# Revit family: Projection_Screen-Draper_Inc.-Targa
name_source: partatom
category: Specialty Equipment
units: mm (PartAtom-declared; Revit-internal decimal feet)

## family parameters
Always vertical = Yes
Classification Number = 23.85.10.14.31
Cut with Voids When Loaded = No
Enable Cutting in Views = No
Maintain Annotation Orientation = No
Part Type = Normal
Room Calculation Point = No
Round Connector Dimension = Use Diameter
Shared = No
Work Plane-Based = No

## types (80) — shared parameters
Apparent Load = 132 VA
Case Material = Paint - Draper - White
Default Elevation = 0"
Depth = 5 1/4"
Description = Projection Screen
Frequency = 60 Hz
Manufacturer = Draper Inc.
Model = Targa
Number of Poles = 1
Product Documentation Link = http://www.draperinc.com
Product Name = Targa  Electric Projection Screen
Product Page URL = http://www.draperinc.com
Projection Screen Material = Fabric - Draper - CH1900E - Pearl White
URL = http://www.DraperInc.com
Width = 4 3/4"

## per-type parameters (varying)
| type | Border | Image Area | Image Height | Image Height Constraint | Image Length | Image Length Constraint | Length | Overall Size | Screen | Screen Drop | Voltage |
| AV Format - 12’  x 12’  - 220 V | No | 144" x 144" | 12' - 0" | 11' - 11 3/4" | 12' - 0" | 11' - 11 3/4" | 12' - 7" | 144" x 144" | 12' - 0" | 12' - 0" | 220 V |
| AV Format - 9’  x 12’  - 220 V | No | 108" x 144" | 9' - 0" | 8' - 11 3/4" | 12' - 0" | 11' - 11 3/4" | 12' - 7" | 108" x 144" | 12' - 0" | 9' - 0" | 220 V |
| AV Format - 10’  x 10’  - 220 V | No | 120" x 120" | 10' - 0" | 9' - 11 3/4" | 10' - 0" | 9' - 11 3/4" | 10' - 7" | 120" x 120" | 10' - 0" | 10' - 0" | 220 V |
| AV Format - 8’  x 10’  - 220 V | No | 96" x 120" | 8' - 0" | 7' - 11 3/4" | 10' - 0" | 9' - 11 3/4" | 10' - 7" | 96" x 120" | 10' - 0" | 8' - 0" | 220 V |
| AV Format - 9’  x 9’  - 220 V | No | 108" x 108" | 9' - 0" | 8' - 11 3/4" | 9' - 0" | 8' - 11 3/4" | 9' - 7" | 108" x 108" | 9' - 0" | 9' - 0" | 220 V |
| AV Format - 7’  x 9’  - 220 V | No | 84" x 108" | 7' - 0" | 6' - 11 3/4" | 9' - 0" | 8' - 11 3/4" | 9' - 7" | 84" x 108" | 9' - 0" | 7' - 0" | 220 V |
| AV Format - 96" x 96" - 220 V | No | 96" x 96" | 8' - 0" | 7' - 11 3/4" | 8' - 0" | 7' - 11 3/4" | 8' - 7" | 96" x 96" | 8' - 0" | 8' - 0" | 220 V |
| AV Format - 72" x 96" - 220 V | No | 72" x 96" | 6' - 0" | 5' - 11 3/4" | 8' - 0" | 7' - 11 3/4" | 8' - 7" | 72" x 96" | 8' - 0" | 6' - 0" | 220 V |
| AV Format - 84" x 84" - 220 V | No | 84" x 84" | 7' - 0" | 6' - 11 3/4" | 7' - 0" | 6' - 11 3/4" | 7' - 6 1/2" | 84" x 84" | 7' - 0" | 7' - 0" | 220 V |
| AV Format - 70" x 70" - 220 V | No | 70" x 70" | 5' - 10" | 5' - 9 3/4" | 5' - 10" | 5' - 9 3/4" | 6' - 4 1/2" | 70" x 70" | 5' - 10" | 5' - 10" | 220 V |
| AV Format - 60" x 60" - 220 V | No | 60" x 60" | 5' - 0" | 4' - 11 3/4" | 5' - 0" | 4' - 11 3/4" | 5' - 6 1/2" | 60" x 60" | 5' - 0" | 5' - 0" | 220 V |
| AV Format - 50" x 50" - 220 V | No | 50" x 50" | 4' - 2" | 4' - 1 3/4" | 4' - 2" | 4' - 1 3/4" | 4' - 8 1/2" | 50" x 50" | 4' - 2" | 4' - 2" | 220 V |
| 16:10 Format - 189" - 220 V | Yes | 100" x 160" | 8' - 4" | 8' - 4" | 13' - 4" | 13' - 4" | 14' - 3" | 105" x 164" | 13' - 8" | 8' - 9" | 220 V |
| 16:10 Format - 165" - 220 V | Yes | 87 1/2" x 140" | 7' - 3 1/2" | 7' - 3 1/2" | 11' - 8" | 11' - 8" | 12' - 7" | 92 1/2" x 144" | 12' - 0" | 7' - 8 1/2" | 220 V |
| 16:10 Format - 137" - 220 V | Yes | 72 1/2" x 116" | 6' - 0 1/2" | 6' - 0 1/2" | 9' - 8" | 9' - 8" | 10' - 7" | 76 1/2" x 120" | 10' - 0" | 6' - 4 1/2" | 220 V |
| 16:10 Format - 123" - 220 V | Yes | 65" x 104" | 5' - 5" | 5' - 5" | 8' - 8" | 8' - 8" | 9' - 7" | 69" x 108" | 9' - 0" | 5' - 9" | 220 V |
| 16:10 Format - 109" - 220 V | Yes | 57 1/2" x 92" | 4' - 9 1/2" | 4' - 9 1/2" | 7' - 8" | 7' - 8" | 8' - 7" | 69 1/2" x 96" | 8' - 0" | 5' - 9 1/2" | 220 V |
| 16:10 Format - 94" - 220 V | Yes | 50" x 80" | 4' - 2" | 4' - 2" | 6' - 8" | 6' - 8" | 7' - 6 1/2" | 62" x 83 1/2" | 6' - 11 1/2" | 5' - 2" | 220 V |
| 16:10 Format - 85" - 220 V | Yes | 45" x 72" | 3' - 9" | 3' - 9" | 6' - 0" | 6' - 0" | 6' - 9" | 57" x 74" | 6' - 2" | 4' - 9" | 220 V |
| 16:10 Format - 76" - 220 V | Yes | 40" x 64" | 3' - 4" | 3' - 4" | 5' - 4" | 5' - 4" | 6' - 4 1/2" | 52" x 69 1/2" | 5' - 9 1/2" | 4' - 4" | 220 V |
| 16:10 Format - 67" - 220 V | Yes | 35 ¬" x 56 1/2" | 2' - 11 1/4" | 2' - 11 1/4" | 4' - 8 1/2" | 4' - 8 1/2" | 5' - 6 1/2" | 47 ¬" x 59 1/2" | 4' - 11 1/2" | 3' - 11 1/4" | 220 V |
| 16:9 HDTV Format - 184" - 220 V | Yes | 90" x 160" | 7' - 6" | 7' - 6" | 13' - 4" | 13' - 4" | 14' - 3" | 95" x 164" | 13' - 8" | 7' - 11" | 220 V |
| 16:9 HDTV Format - 161" - 220 V | Yes | 79" x 140" | 6' - 7" | 6' - 7" | 11' - 8" | 11' - 8" | 12' - 7" | 84" x 144" | 12' - 0" | 7' - 0" | 220 V |
| 16:9 HDTV Format - 133" - 220 V | Yes | 65" x 116" | 5' - 5" | 5' - 5" | 9' - 8" | 9' - 8" | 10' - 7" | 69" x 120" | 10' - 0" | 5' - 9" | 220 V |
| 16:9 HDTV Format - 119" - 220 V | Yes | 58" x 104" | 4' - 10" | 4' - 10" | 8' - 8" | 8' - 8" | 9' - 7" | 62" x 108" | 9' - 0" | 5' - 2" | 220 V |
| 16:9 HDTV Format - 110" - 220 V | Yes | 54" x 96" | 4' - 6" | 4' - 6" | 8' - 0" | 8' - 0" | 8' - 11" | 66" x 100" | 8' - 4" | 5' - 6" | 220 V |
| 16:9 HDTV Format - 106" - 220 V | Yes | 52" x 92" | 4' - 4" | 4' - 4" | 7' - 8" | 7' - 8" | 8' - 7" | 64" x 96" | 8' - 0" | 5' - 4" | 220 V |
| 16:9 HDTV Format - 100" - 220 V | Yes | 49" x 87" | 4' - 1" | 4' - 1" | 7' - 3" | 7' - 3" | 8' - 2" | 61" x 91" | 7' - 7" | 5' - 1" | 220 V |
| 16:9 HDTV Format - 92" - 220 V | Yes | 45" x 80" | 3' - 9" | 3' - 9" | 6' - 8" | 6' - 8" | 7' - 6 1/2" | 57" x 83 1/2" | 6' - 11 1/2" | 4' - 9" | 220 V |
| 16:9 HDTV Format - 82" - 220 V | Yes | 40 1/2" x 72" | 3' - 4 1/2" | 3' - 4 1/2" | 6' - 0" | 6' - 0" | 6' - 9" | 52 1/2" x 74" | 6' - 2" | 4' - 4 1/2" | 220 V |
| 16:9 HDTV Format - 73" - 220 V | Yes | 36" x 64" | 3' - 0" | 3' - 0" | 5' - 4" | 5' - 4" | 6' - 4 1/2" | 48" x 69 1/2" | 5' - 9 1/2" | 4' - 0" | 220 V |
| 16:9 HDTV Format - 65" - 220 V | Yes | 31 ‘ " x 56 1/2" | 2' - 6 3/4" | 2' - 6 3/4" | 4' - 8 1/2" | 4' - 8 1/2" | 5' - 6 1/2" | 43 ‘ " x 59 1/2" | 4' - 11 1/2" | 3' - 7 3/4" | 220 V |
| 4:3 NTSC/PAL Video Format - 200" - 220 V | Yes | 118" x 158" | 9' - 10" | 9' - 10" | 13' - 2" | 13' - 2" | 14' - 1" | 123" x 162" | 13' - 6" | 10' - 3" | 220 V |
| 4:3 NTSC/PAL Video Format - 15’  - 220 V | Yes | 105" x 140" | 8' - 9" | 8' - 9" | 11' - 8" | 11' - 8" | 12' - 7" | 109" x 144" | 12' - 0" | 9' - 1" | 220 V |
| 4:3 NTSC/PAL Video Format - 150" - 220 V | Yes | 87" x 116" | 7' - 3" | 7' - 3" | 9' - 8" | 9' - 8" | 10' - 7" | 92" x 120" | 10' - 0" | 7' - 8" | 220 V |
| 4:3 NTSC/PAL Video Format - 11’  - 220 V | Yes | 78" x 104" | 6' - 6" | 6' - 6" | 8' - 8" | 8' - 8" | 9' - 7" | 83" x 108" | 9' - 0" | 6' - 11" | 220 V |
| 4:3 NTSC/PAL Video Format - 10’  - 220 V | Yes | 69" x 92" | 5' - 9" | 5' - 9" | 7' - 8" | 7' - 8" | 8' - 7" | 73" x 96" | 8' - 0" | 6' - 1" | 220 V |
| 4:3 NTSC/PAL Video Format - 100" - 220 V | Yes | 60" x 80" | 5' - 0" | 5' - 0" | 6' - 8" | 6' - 8" | 7' - 6 1/2" | 64" x 83 1/2" | 6' - 11 1/2" | 5' - 4" | 220 V |
| 4:3 NTSC/PAL Video Format - 7’  - 220 V | Yes | 50" x 66 1/2" | 4' - 2" | 4' - 2" | 5' - 6 1/2" | 5' - 6 1/2" | 6' - 4 1/2" | 53 1/2" x 69 1/2" | 5' - 9 1/2" | 4' - 5 1/2" | 220 V |
| 4:3 NTSC/PAL Video Format - 6’  - 220 V | Yes | 42 1/2" x 56 1/2" | 3' - 6 1/2" | 3' - 6 1/2" | 4' - 8 1/2" | 4' - 8 1/2" | 5' - 6 1/2" | 46 1/2" x 59 1/2" | 4' - 11 1/2" | 3' - 10 1/2" | 110 V |
| AV Format - 12’  x 12’  - 110 V | No | 144" x 144" | 12' - 0" | 11' - 11 3/4" | 12' - 0" | 11' - 11 3/4" | 12' - 7" | 144" x 144" | 12' - 0" | 12' - 0" | 110 V |
| AV Format - 9’  x 12’  - 110 V | No | 108" x 144" | 9' - 0" | 8' - 11 3/4" | 12' - 0" | 11' - 11 3/4" | 12' - 7" | 108" x 144" | 12' - 0" | 9' - 0" | 110 V |
| AV Format - 10’  x 10’  - 110 V | No | 120" x 120" | 10' - 0" | 9' - 11 3/4" | 10' - 0" | 9' - 11 3/4" | 10' - 7" | 120" x 120" | 10' - 0" | 10' - 0" | 110 V |
| AV Format - 8’  x 10’  - 110 V | No | 96" x 120" | 8' - 0" | 7' - 11 3/4" | 10' - 0" | 9' - 11 3/4" | 10' - 7" | 96" x 120" | 10' - 0" | 8' - 0" | 110 V |
| AV Format - 9’  x 9’  - 110 V | No | 108" x 108" | 9' - 0" | 8' - 11 3/4" | 9' - 0" | 8' - 11 3/4" | 9' - 7" | 108" x 108" | 9' - 0" | 9' - 0" | 110 V |
| AV Format - 7’  x 9’  - 110 V | No | 84" x 108" | 7' - 0" | 6' - 11 3/4" | 9' - 0" | 8' - 11 3/4" | 9' - 7" | 84" x 108" | 9' - 0" | 7' - 0" | 110 V |
| AV Format - 96" x 96" - 110 V | No | 96" x 96" | 8' - 0" | 7' - 11 3/4" | 8' - 0" | 7' - 11 3/4" | 8' - 7" | 96" x 96" | 8' - 0" | 8' - 0" | 110 V |
| AV Format - 72" x 96" - 110 V | No | 72" x 96" | 6' - 0" | 5' - 11 3/4" | 8' - 0" | 7' - 11 3/4" | 8' - 7" | 72" x 96" | 8' - 0" | 6' - 0" | 110 V |
| AV Format - 84" x 84" - 110 V | No | 84" x 84" | 7' - 0" | 6' - 11 3/4" | 7' - 0" | 6' - 11 3/4" | 7' - 6 1/2" | 84" x 84" | 7' - 0" | 7' - 0" | 110 V |
| AV Format - 70" x 70" - 110 V | No | 70" x 70" | 5' - 10" | 5' - 9 3/4" | 5' - 10" | 5' - 9 3/4" | 6' - 4 1/2" | 70" x 70" | 5' - 10" | 5' - 10" | 110 V |
| AV Format - 60" x 60" - 110 V | No | 60" x 60" | 5' - 0" | 4' - 11 3/4" | 5' - 0" | 4' - 11 3/4" | 5' - 6 1/2" | 60" x 60" | 5' - 0" | 5' - 0" | 110 V |
| AV Format - 50" x 50" - 110 V | No | 50" x 50" | 4' - 2" | 4' - 1 3/4" | 4' - 2" | 4' - 1 3/4" | 4' - 8 1/2" | 50" x 50" | 4' - 2" | 4' - 2" | 110 V |
| 16:10 Format - 189" - 110 V | Yes | 100" x 160" | 8' - 4" | 8' - 4" | 13' - 4" | 13' - 4" | 14' - 3" | 105" x 164" | 13' - 8" | 8' - 9" | 110 V |
| 16:10 Format - 165" - 110 V | Yes | 87 1/2" x 140" | 7' - 3 1/2" | 7' - 3 1/2" | 11' - 8" | 11' - 8" | 12' - 7" | 92 1/2" x 144" | 12' - 0" | 7' - 8 1/2" | 110 V |
| 16:10 Format - 137" - 110 V | Yes | 72 1/2" x 116" | 6' - 0 1/2" | 6' - 0 1/2" | 9' - 8" | 9' - 8" | 10' - 7" | 76 1/2" x 120" | 10' - 0" | 6' - 4 1/2" | 110 V |
| 16:10 Format - 123" - 110 V | Yes | 65" x 104" | 5' - 5" | 5' - 5" | 8' - 8" | 8' - 8" | 9' - 7" | 69" x 108" | 9' - 0" | 5' - 9" | 110 V |
| 16:10 Format - 109" - 110 V | Yes | 57 1/2" x 92" | 4' - 9 1/2" | 4' - 9 1/2" | 7' - 8" | 7' - 8" | 8' - 7" | 69 1/2" x 96" | 8' - 0" | 5' - 9 1/2" | 110 V |
| 16:10 Format - 94" - 110 V | Yes | 50" x 80" | 4' - 2" | 4' - 2" | 6' - 8" | 6' - 8" | 7' - 6 1/2" | 62" x 83 1/2" | 6' - 11 1/2" | 5' - 2" | 110 V |
| 16:10 Format - 85" - 110 V | Yes | 45" x 72" | 3' - 9" | 3' - 9" | 6' - 0" | 6' - 0" | 6' - 9" | 57" x 74" | 6' - 2" | 4' - 9" | 110 V |
| 16:10 Format - 76" - 110 V | Yes | 40" x 64" | 3' - 4" | 3' - 4" | 5' - 4" | 5' - 4" | 6' - 4 1/2" | 52" x 69 1/2" | 5' - 9 1/2" | 4' - 4" | 110 V |
| 16:10 Format - 67" - 110 V | Yes | 35 ¬" x 56 1/2" | 2' - 11 1/4" | 2' - 11 1/4" | 4' - 8 1/2" | 4' - 8 1/2" | 5' - 6 1/2" | 47 ¬" x 59 1/2" | 4' - 11 1/2" | 3' - 11 1/4" | 110 V |
| 16:9 HDTV Format - 184" - 110 V | Yes | 90" x 160" | 7' - 6" | 7' - 6" | 13' - 4" | 13' - 4" | 14' - 3" | 95" x 164" | 13' - 8" | 7' - 11" | 110 V |
| 16:9 HDTV Format - 161" - 110 V | Yes | 79" x 140" | 6' - 7" | 6' - 7" | 11' - 8" | 11' - 8" | 12' - 7" | 84" x 144" | 12' - 0" | 7' - 0" | 110 V |
| 16:9 HDTV Format - 133" - 110 V | Yes | 65" x 116" | 5' - 5" | 5' - 5" | 9' - 8" | 9' - 8" | 10' - 7" | 69" x 120" | 10' - 0" | 5' - 9" | 110 V |
| 16:9 HDTV Format - 119" - 110 V | Yes | 58" x 104" | 4' - 10" | 4' - 10" | 8' - 8" | 8' - 8" | 9' - 7" | 62" x 108" | 9' - 0" | 5' - 2" | 110 V |
| 16:9 HDTV Format - 110" - 110 V | Yes | 54" x 96" | 4' - 6" | 4' - 6" | 8' - 0" | 8' - 0" | 8' - 11" | 66" x 100" | 8' - 4" | 5' - 6" | 110 V |
| 16:9 HDTV Format - 106" - 110 V | Yes | 52" x 92" | 4' - 4" | 4' - 4" | 7' - 8" | 7' - 8" | 8' - 7" | 64" x 96" | 8' - 0" | 5' - 4" | 110 V |
| 16:9 HDTV Format - 100" - 110 V | Yes | 49" x 87" | 4' - 1" | 4' - 1" | 7' - 3" | 7' - 3" | 8' - 2" | 61" x 91" | 7' - 7" | 5' - 1" | 110 V |
| 16:9 HDTV Format - 92" - 110 V | Yes | 45" x 80" | 3' - 9" | 3' - 9" | 6' - 8" | 6' - 8" | 7' - 6 1/2" | 57" x 83 1/2" | 6' - 11 1/2" | 4' - 9" | 110 V |
| 16:9 HDTV Format - 82" - 110 V | Yes | 40 1/2" x 72" | 3' - 4 1/2" | 3' - 4 1/2" | 6' - 0" | 6' - 0" | 6' - 9" | 52 1/2" x 74" | 6' - 2" | 4' - 4 1/2" | 110 V |
| 16:9 HDTV Format - 73" - 110 V | Yes | 36" x 64" | 3' - 0" | 3' - 0" | 5' - 4" | 5' - 4" | 6' - 4 1/2" | 48" x 69 1/2" | 5' - 9 1/2" | 4' - 0" | 110 V |
| 16:9 HDTV Format - 65" - 110 V | Yes | 31 ‘ " x 56 1/2" | 2' - 6 3/4" | 2' - 6 3/4" | 4' - 8 1/2" | 4' - 8 1/2" | 5' - 6 1/2" | 43 ‘ " x 59 1/2" | 4' - 11 1/2" | 3' - 7 3/4" | 110 V |
| 4:3 NTSC/PAL Video Format - 200" - 110 V | Yes | 118" x 158" | 9' - 10" | 9' - 10" | 13' - 2" | 13' - 2" | 14' - 1" | 123" x 162" | 13' - 6" | 10' - 3" | 110 V |
| 4:3 NTSC/PAL Video Format - 15’  - 110 V | Yes | 105" x 140" | 8' - 9" | 8' - 9" | 11' - 8" | 11' - 8" | 12' - 7" | 109" x 144" | 12' - 0" | 9' - 1" | 110 V |
| 4:3 NTSC/PAL Video Format - 150" - 110 V | Yes | 87" x 116" | 7' - 3" | 7' - 3" | 9' - 8" | 9' - 8" | 10' - 7" | 92" x 120" | 10' - 0" | 7' - 8" | 110 V |
| 4:3 NTSC/PAL Video Format - 11’  - 110 V | Yes | 78" x 104" | 6' - 6" | 6' - 6" | 8' - 8" | 8' - 8" | 9' - 7" | 83" x 108" | 9' - 0" | 6' - 11" | 110 V |
| 4:3 NTSC/PAL Video Format - 10’  - 110 V | Yes | 69" x 92" | 5' - 9" | 5' - 9" | 7' - 8" | 7' - 8" | 8' - 7" | 73" x 96" | 8' - 0" | 6' - 1" | 110 V |
| 4:3 NTSC/PAL Video Format - 100" - 110 V | Yes | 60" x 80" | 5' - 0" | 5' - 0" | 6' - 8" | 6' - 8" | 7' - 6 1/2" | 64" x 83 1/2" | 6' - 11 1/2" | 5' - 4" | 110 V |
| 4:3 NTSC/PAL Video Format - 7’  - 110 V | Yes | 50" x 66 1/2" | 4' - 2" | 4' - 2" | 5' - 6 1/2" | 5' - 6 1/2" | 6' - 4 1/2" | 53 1/2" x 69 1/2" | 5' - 9 1/2" | 4' - 5 1/2" | 110 V |
| 4:3 NTSC/PAL Video Format - 6’  - 110 V | Yes | 42 1/2" x 56 1/2" | 3' - 6 1/2" | 3' - 6 1/2" | 4' - 8 1/2" | 4' - 8 1/2" | 5' - 6 1/2" | 46 1/2" x 59 1/2" | 4' - 11 1/2" | 3' - 10 1/2" | 110 V |

## geometry (parser evidence)
native form markers: Blend x2, Sweep x2
no freeform markers — native parametric forms only
